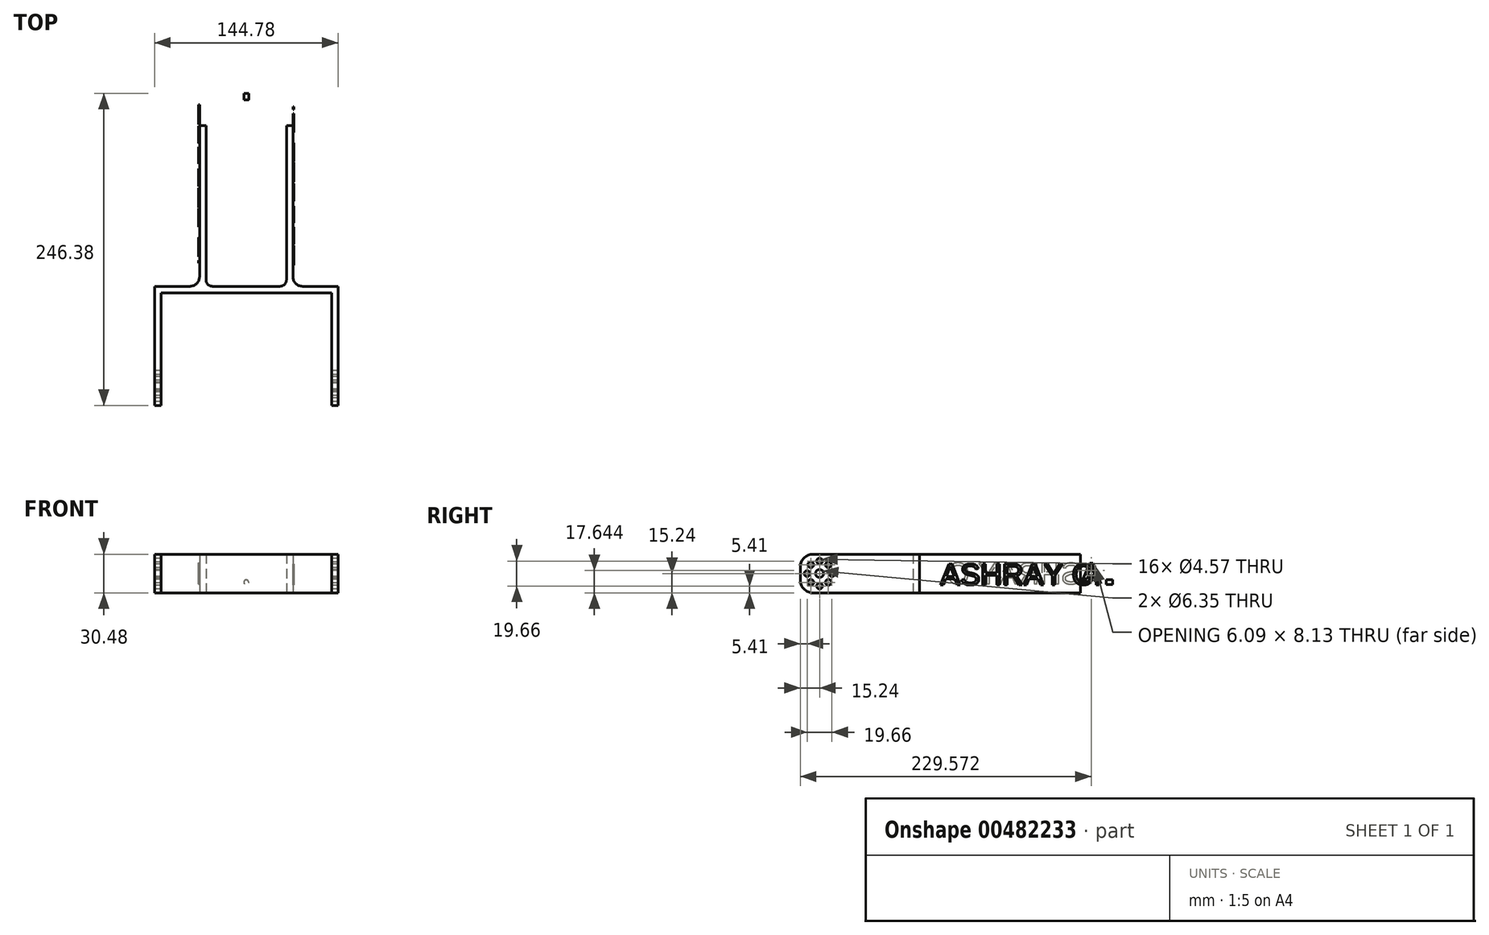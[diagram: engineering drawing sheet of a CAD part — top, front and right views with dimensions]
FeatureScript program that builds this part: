
annotation { "Feature Type Name" : "Feature", "Feature Type Description" : "" }
export const myFeature = defineFeature(function(context is Context, id is Id, definition is map)
    precondition{}
    {
        {
            var Q0;
            Q0=qCreatedBy(makeId("Top.planeOp"),FACE);
            var sketch = newSketch(context, id + "F0", { "sketchPlane" : qUnion([Q0])});
            skLineSegment(sketch, "E0.bottom", {"start": v(67.31, -2.54) * mm, "end": v(-67.31, -2.54) * mm});
            skLineSegment(sketch, "E0.top", {"start": v(67.31, 2.54) * mm, "end": v(-67.31, 2.54) * mm});
            skLineSegment(sketch, "E0.left", {"start": v(67.31, -2.54) * mm, "end": v(67.31, 2.54) * mm});
            skLineSegment(sketch, "E0.right", {"start": v(-67.31, -2.54) * mm, "end": v(-67.31, 2.54) * mm});
            skPoint(sketch, "E0.middle", {"position": v(0, 0) * mm});
            skLineSegment(sketch, "E1.bottom", {"start": v(-67.3, -91.44) * mm, "end": v(-72.4, -91.44) * mm});
            skLineSegment(sketch, "E1.top", {"start": v(-67.31, 154.94) * mm, "end": v(-72.4, 154.94) * mm});
            skLineSegment(sketch, "E1.left", {"start": v(-67.31, -91.44) * mm, "end": v(-67.31, 154.94) * mm});
            skLineSegment(sketch, "E1.right", {"start": v(-72.4, -91.44) * mm, "end": v(-72.4, 154.94) * mm});
            skLineSegment(sketch, "E2.bottom", {"start": v(67.31, -91.44) * mm, "end": v(72.4, -91.44) * mm});
            skLineSegment(sketch, "E2.top", {"start": v(67.31, 154.94) * mm, "end": v(72.4, 154.94) * mm});
            skLineSegment(sketch, "E2.left", {"start": v(67.31, -91.44) * mm, "end": v(67.31, 154.94) * mm});
            skLineSegment(sketch, "E2.right", {"start": v(72.4, -91.44) * mm, "end": v(72.4, 154.94) * mm});
            skLineSegment(sketch, "E3.bottom", {"start": v(-36.83, 2.54) * mm, "end": v(-31.75, 2.54) * mm});
            skLineSegment(sketch, "E3.top", {"start": v(-36.83, 154.94) * mm, "end": v(-31.75, 154.94) * mm});
            skLineSegment(sketch, "E3.left", {"start": v(-36.83, 2.54) * mm, "end": v(-36.83, 154.94) * mm});
            skLineSegment(sketch, "E3.right", {"start": v(-31.75, 2.54) * mm, "end": v(-31.75, 154.94) * mm});
            skLineSegment(sketch, "E4.bottom", {"start": v(31.75, 2.54) * mm, "end": v(36.83, 2.54) * mm});
            skLineSegment(sketch, "E4.top", {"start": v(31.75, 154.94) * mm, "end": v(36.83, 154.94) * mm});
            skLineSegment(sketch, "E4.left", {"start": v(31.75, 2.54) * mm, "end": v(31.75, 154.94) * mm});
            skLineSegment(sketch, "E4.right", {"start": v(36.83, 2.54) * mm, "end": v(36.83, 154.94) * mm});
            skLineSegment(sketch, "E5", {"start": v(-36.83, 154.94) * mm, "end": v(36.83, 154.94) * mm});
            skLineSegment(sketch, "E6", {"start": v(-67.31, 2.54) * mm, "end": v(-72.4, 2.54) * mm});
            skLineSegment(sketch, "E7", {"start": v(67.31, 2.54) * mm, "end": v(72.4, 2.54) * mm});
            skSolve(sketch);
        }
        {
            var Q0;
            Q0=makeQuery(id+"F0.imprint","IMPRINT",FACE,{"disambiguationData":[TD([[makeQuery(id+"F0.imprint","IMPRINT",EDGE,{"derivedFrom":sQuery(id+"F0.wireOp",EDGE,"E3.top")}),-1.0]])]});
            var Q1;
            Q1=makeQuery(id+"F0.imprint","IMPRINT",FACE,{"disambiguationData":[TD([[makeQuery(id+"F0.imprint","IMPRINT",EDGE,{"derivedFrom":sQuery(id+"F0.wireOp",EDGE,"E4.top")}),-1.0]])]});
            var Q2;
            Q2=makeQuery(id+"F0.imprint","IMPRINT",FACE,{"disambiguationData":[TD([[makeQuery(id+"F0.imprint","IMPRINT",EDGE,{"derivedFrom":sQuery(id+"F0.wireOp",EDGE,"E0.bottom")}),-1.0]])]});
            var Q3;
            {var subQ1=sQuery(id+"F0.wireOp",EDGE,"E0.left");Q3=makeQuery(id+"F0.imprint","IMPRINT",FACE,{"disambiguationData":[TD([[makeQuery(id+"F0.imprint","IMPRINT",EDGE,{"derivedFrom":subQ1}),-1.0]])]});}
            var Q4;
            {var subQ1=sQuery(id+"F0.wireOp",EDGE,"E0.right");Q4=makeQuery(id+"F0.imprint","IMPRINT",FACE,{"disambiguationData":[TD([[makeQuery(id+"F0.imprint","IMPRINT",EDGE,{"derivedFrom":subQ1}),1.0]])]});}
            extrude(context, id + "F1", {"entities" : qUnion([Q0, Q1, Q2, Q3, Q4]), "depth" : 30.48 * mm});
        }
        {
            var Q0;
            Q0=makeQuery(id+"F1.opExtrude","SWEPT_FACE",FACE,{"disambiguationData":[OSD([sQuery(id+"F0.wireOp",EDGE,"E3.right")])]});
            var sketch = newSketch(context, id + "F2", { "sketchPlane" : qUnion([Q0])});
            skLineSegment(sketch, "E8.bottom", {"start": v(154.94, 30.48) * mm, "end": v(149.86, 30.48) * mm});
            skLineSegment(sketch, "E8.top", {"start": v(154.94, 0) * mm, "end": v(149.86, 0) * mm});
            skLineSegment(sketch, "E8.left", {"start": v(154.94, 30.48) * mm, "end": v(154.94, 0) * mm});
            skLineSegment(sketch, "E8.right", {"start": v(149.86, 30.48) * mm, "end": v(149.86, 0) * mm});
            skSolve(sketch);
        }
        {
            var Q0;
            Q0=makeQuery(id+"F2.imprint","IMPRINT",FACE,{"disambiguationData":[TD([[makeQuery(id+"F2.imprint","IMPRINT",EDGE,{"derivedFrom":sQuery(id+"F2.wireOp",EDGE,"E8.bottom")}),-1.0]])]});
            extrude(context, id + "F3", {"entities" : qUnion([Q0]), "operationType" : NewBodyOperationType.ADD, "depth" : 66.04 * mm});
        }
        {
            var Q0;
            Q0=makeQuery(id+"F1.opExtrude","SWEPT_EDGE",EDGE,{"disambiguationData":[OSD([sQuery(id+"F0.wireOp",EDGE,"E0.top"),sQuery(id+"F0.wireOp",EDGE,"E3.left")])]});
            var Q1;
            Q1=makeQuery(id+"F1.opExtrude","SWEPT_EDGE",EDGE,{"disambiguationData":[OSD([sQuery(id+"F0.wireOp",EDGE,"E0.top"),sQuery(id+"F0.wireOp",EDGE,"E4.right")])]});
            fillet(context, id + "F4", {"entities" : qUnion([Q0, Q1]), "radius" : 7.62 * mm, "tangentPropagation" : true, "allowEdgeOverflow" : false});
        }
        {
            var Q0;
            Q0=makeQuery(id+"F1.opExtrude","SWEPT_EDGE",EDGE,{"disambiguationData":[OSD([sQuery(id+"F0.wireOp",EDGE,"E0.top"),sQuery(id+"F0.wireOp",EDGE,"E3.right")])]});
            var Q1;
            Q1=makeQuery(id+"F1.opExtrude","SWEPT_EDGE",EDGE,{"disambiguationData":[OSD([sQuery(id+"F0.wireOp",EDGE,"E0.top"),sQuery(id+"F0.wireOp",EDGE,"E4.left")])]});
            fillet(context, id + "F5", {"entities" : qUnion([Q0, Q1]), "radius" : 5.08 * mm, "tangentPropagation" : true, "allowEdgeOverflow" : false});
        }
        {
            var Q0;
            Q0=makeQuery(id+"F1.opExtrude","SWEPT_FACE",FACE,{"disambiguationData":[OSD([sQuery(id+"F0.wireOp",EDGE,"E1.right")])]});
            var sketch = newSketch(context, id + "F6", { "sketchPlane" : qUnion([Q0])});
            skCircle(sketch, "E9", {"center": v(76.2, 15.24) * mm, "radius": 12.7 * mm});
            skCircle(sketch, "E10", {"center": v(66.37, 15.24) * mm, "radius": 2.29 * mm});
            skCircle(sketch, "E11", {"center": v(76.2, 25.07) * mm, "radius": 2.29 * mm});
            skCircle(sketch, "E12", {"center": v(86.03, 15.24) * mm, "radius": 2.29 * mm});
            skCircle(sketch, "E13", {"center": v(76.2, 5.41) * mm, "radius": 2.29 * mm});
            skCircle(sketch, "E14", {"center": v(76.2, 15.24) * mm, "radius": 3.18 * mm});
            skLineSegment(sketch, "E15", {"start": v(66.37, 15.24) * mm, "end": v(86.03, 15.24) * mm});
            skLineSegment(sketch, "E16", {"start": v(76.2, 25.07) * mm, "end": v(76.2, 5.41) * mm});
            skCircle(sketch, "E17", {"center": v(69.25, 8.29) * mm, "radius": 2.29 * mm});
            skCircle(sketch, "E18", {"center": v(83.15, 22.2) * mm, "radius": 2.29 * mm});
            skCircle(sketch, "E19", {"center": v(69.25, 22.2) * mm, "radius": 2.29 * mm});
            skCircle(sketch, "E20", {"center": v(83.15, 8.29) * mm, "radius": 2.29 * mm});
            skLineSegment(sketch, "E21", {"start": v(69.25, 8.29) * mm, "end": v(83.15, 22.2) * mm});
            skLineSegment(sketch, "E22", {"start": v(69.25, 22.2) * mm, "end": v(83.15, 8.29) * mm});
            skSolve(sketch);
        }
        {
            var Q0;
            Q0=makeQuery(id+"F6.imprint","IMPRINT",FACE,{"disambiguationData":[TD([[makeQuery(id+"F6.imprint","IMPRINT",EDGE,{"derivedFrom":sQuery(id+"F6.wireOp",EDGE,"E18")}),1.0]])]});
            var Q1;
            Q1=makeQuery(id+"F6.imprint","IMPRINT",FACE,{"disambiguationData":[TD([[makeQuery(id+"F6.imprint","IMPRINT",EDGE,{"derivedFrom":sQuery(id+"F6.wireOp",EDGE,"E11")}),1.0]])]});
            var Q2;
            Q2=makeQuery(id+"F6.imprint","IMPRINT",FACE,{"disambiguationData":[TD([[makeQuery(id+"F6.imprint","IMPRINT",EDGE,{"derivedFrom":sQuery(id+"F6.wireOp",EDGE,"E19")}),1.0]])]});
            var Q3;
            Q3=makeQuery(id+"F6.imprint","IMPRINT",FACE,{"disambiguationData":[TD([[makeQuery(id+"F6.imprint","IMPRINT",EDGE,{"derivedFrom":sQuery(id+"F6.wireOp",EDGE,"E10")}),1.0]])]});
            var Q4;
            Q4=makeQuery(id+"F6.imprint","IMPRINT",FACE,{"disambiguationData":[TD([[makeQuery(id+"F6.imprint","IMPRINT",EDGE,{"derivedFrom":sQuery(id+"F6.wireOp",EDGE,"E17")}),1.0]])]});
            var Q5;
            Q5=makeQuery(id+"F6.imprint","IMPRINT",FACE,{"disambiguationData":[TD([[makeQuery(id+"F6.imprint","IMPRINT",EDGE,{"derivedFrom":sQuery(id+"F6.wireOp",EDGE,"E13")}),1.0]])]});
            var Q6;
            Q6=makeQuery(id+"F6.imprint","IMPRINT",FACE,{"disambiguationData":[TD([[makeQuery(id+"F6.imprint","IMPRINT",EDGE,{"derivedFrom":sQuery(id+"F6.wireOp",EDGE,"E20")}),1.0]])]});
            var Q7;
            Q7=makeQuery(id+"F6.imprint","IMPRINT",FACE,{"disambiguationData":[TD([[makeQuery(id+"F6.imprint","IMPRINT",EDGE,{"derivedFrom":sQuery(id+"F6.wireOp",EDGE,"E12")}),1.0]])]});
            var Q8;
            {var subQ0=sQuery(id+"F6.wireOp",EDGE,"E16");var subQ1=sQuery(id+"F6.wireOp",EDGE,"E14");var subQ2=makeQuery(id+"F6.imprint","INTERSECT",VERTEX,{"disambiguationData":[OD(1.0)],"derivedFrom":[subQ1,subQ0]});Q8=makeQuery(id+"F6.imprint","IMPRINT",FACE,{"disambiguationData":[TD([[makeQuery(id+"F6.imprint","IMPRINT",EDGE,{"disambiguationData":[TD([[subQ2,-1.0]])],"derivedFrom":subQ1}),1.0]])]});}
            var Q9;
            {var subQ0=sQuery(id+"F6.wireOp",EDGE,"E15");var subQ1=sQuery(id+"F6.wireOp",EDGE,"E14");var subQ2=makeQuery(id+"F6.imprint","INTERSECT",VERTEX,{"disambiguationData":[OD(0.0)],"derivedFrom":[subQ1,subQ0]});Q9=makeQuery(id+"F6.imprint","IMPRINT",FACE,{"disambiguationData":[TD([[makeQuery(id+"F6.imprint","IMPRINT",EDGE,{"disambiguationData":[TD([[subQ2,1.0]])],"derivedFrom":subQ1}),1.0]])]});}
            var Q10;
            {var subQ0=sQuery(id+"F6.wireOp",EDGE,"E21");var subQ1=sQuery(id+"F6.wireOp",EDGE,"E14");var subQ2=makeQuery(id+"F6.imprint","INTERSECT",VERTEX,{"disambiguationData":[OD(0.0)],"derivedFrom":[subQ1,subQ0]});Q10=makeQuery(id+"F6.imprint","IMPRINT",FACE,{"disambiguationData":[TD([[makeQuery(id+"F6.imprint","IMPRINT",EDGE,{"disambiguationData":[TD([[subQ2,1.0]])],"derivedFrom":subQ1}),1.0]])]});}
            var Q11;
            {var subQ0=sQuery(id+"F6.wireOp",EDGE,"E21");var subQ1=sQuery(id+"F6.wireOp",EDGE,"E14");var subQ2=makeQuery(id+"F6.imprint","INTERSECT",VERTEX,{"disambiguationData":[OD(0.0)],"derivedFrom":[subQ1,subQ0]});Q11=makeQuery(id+"F6.imprint","IMPRINT",FACE,{"disambiguationData":[TD([[makeQuery(id+"F6.imprint","IMPRINT",EDGE,{"disambiguationData":[TD([[subQ2,-1.0]])],"derivedFrom":subQ1}),1.0]])]});}
            var Q12;
            {var subQ0=sQuery(id+"F6.wireOp",EDGE,"E16");var subQ1=sQuery(id+"F6.wireOp",EDGE,"E14");var subQ2=makeQuery(id+"F6.imprint","INTERSECT",VERTEX,{"disambiguationData":[OD(0.0)],"derivedFrom":[subQ1,subQ0]});Q12=makeQuery(id+"F6.imprint","IMPRINT",FACE,{"disambiguationData":[TD([[makeQuery(id+"F6.imprint","IMPRINT",EDGE,{"disambiguationData":[TD([[subQ2,-1.0]])],"derivedFrom":subQ1}),1.0]])]});}
            var Q13;
            {var subQ0=sQuery(id+"F6.wireOp",EDGE,"E22");var subQ1=sQuery(id+"F6.wireOp",EDGE,"E14");var subQ2=makeQuery(id+"F6.imprint","INTERSECT",VERTEX,{"disambiguationData":[OD(0.0)],"derivedFrom":[subQ1,subQ0]});Q13=makeQuery(id+"F6.imprint","IMPRINT",FACE,{"disambiguationData":[TD([[makeQuery(id+"F6.imprint","IMPRINT",EDGE,{"disambiguationData":[TD([[subQ2,-1.0]])],"derivedFrom":subQ1}),1.0]])]});}
            var Q14;
            {var subQ0=sQuery(id+"F6.wireOp",EDGE,"E15");var subQ1=sQuery(id+"F6.wireOp",EDGE,"E14");var subQ2=makeQuery(id+"F6.imprint","INTERSECT",VERTEX,{"disambiguationData":[OD(1.0)],"derivedFrom":[subQ1,subQ0]});Q14=makeQuery(id+"F6.imprint","IMPRINT",FACE,{"disambiguationData":[TD([[makeQuery(id+"F6.imprint","IMPRINT",EDGE,{"disambiguationData":[TD([[subQ2,-1.0]])],"derivedFrom":subQ1}),1.0]])]});}
            var Q15;
            {var subQ0=sQuery(id+"F6.wireOp",EDGE,"E21");var subQ1=sQuery(id+"F6.wireOp",EDGE,"E14");var subQ2=makeQuery(id+"F6.imprint","INTERSECT",VERTEX,{"disambiguationData":[OD(1.0)],"derivedFrom":[subQ1,subQ0]});Q15=makeQuery(id+"F6.imprint","IMPRINT",FACE,{"disambiguationData":[TD([[makeQuery(id+"F6.imprint","IMPRINT",EDGE,{"disambiguationData":[TD([[subQ2,-1.0]])],"derivedFrom":subQ1}),1.0]])]});}
            extrude(context, id + "F7", {"entities" : qUnion([Q0, Q1, Q2, Q3, Q4, Q5, Q6, Q7, Q8, Q9, Q10, Q11, Q12, Q13, Q14, Q15]), "operationType" : NewBodyOperationType.REMOVE, "oppositeDirection" : true, "depth" : 254 * mm, "offsetDistance" : 25.4 * mm});
        }
        {
            var Q0;
            Q0=makeQuery(id+"F1.opExtrude","CAP_EDGE",EDGE,{"disambiguationData":[OSD([sQuery(id+"F0.wireOp",EDGE,"E2.bottom")])],"isStart":true});
            var Q1;
            Q1=makeQuery(id+"F1.opExtrude","CAP_EDGE",EDGE,{"disambiguationData":[OSD([sQuery(id+"F0.wireOp",EDGE,"E2.bottom")])],"isStart":false});
            var Q2;
            Q2=makeQuery(id+"F1.opExtrude","CAP_EDGE",EDGE,{"disambiguationData":[OSD([sQuery(id+"F0.wireOp",EDGE,"E1.bottom")])],"isStart":true});
            var Q3;
            Q3=makeQuery(id+"F1.opExtrude","CAP_EDGE",EDGE,{"disambiguationData":[OSD([sQuery(id+"F0.wireOp",EDGE,"E1.bottom")])],"isStart":false});
            fillet(context, id + "F8", {"entities" : qUnion([Q0, Q1, Q2, Q3]), "radius" : 10.16 * mm, "tangentPropagation" : true, "allowEdgeOverflow" : false});
        }
        {
            var Q0;
            Q0=makeQuery(id+"F1.opExtrude","SWEPT_FACE",FACE,{"disambiguationData":[OSD([sQuery(id+"F0.wireOp",EDGE,"E4.right")])]});
            var sketch = newSketch(context, id + "F9", { "sketchPlane" : qUnion([Q0])});
            skText(sketch, "E23", { "text": "ASHRAY C.", "fontName": "Arimo-Regular.ttf"});
            const initialGuessF9  = {"E23": [0.01905, 0.00635, 1, 0, 0.01703]};
            skSetInitialGuess(sketch, initialGuessF9);
            skSolve(sketch);
        }
        {
            var Q0;
            Q0=makeQuery(id+"F1.opExtrude","SWEPT_FACE",FACE,{"disambiguationData":[OSD([sQuery(id+"F0.wireOp",EDGE,"E3.left")])]});
            var sketch = newSketch(context, id + "F10", { "sketchPlane" : qUnion([Q0])});
            skText(sketch, "E24", { "text": "ASHRAY C.", "fontName": "Arimo-Regular.ttf"});
            const initialGuessF10  = {"E24": [-0.14605, 0.0071, 1, 0, 0.01703]};
            skSetInitialGuess(sketch, initialGuessF10);
            skSolve(sketch);
        }
        {
            var Q0;
            Q0=makeQuery(id+"F9.imprint","IMPRINT",FACE,{"disambiguationData":[TD([[makeQuery(id+"F9.imprint","IMPRINT",EDGE,{"derivedFrom":sQuery(id+"F9.wireOp",EDGE,"E23.sketch_text.stroke-0")}),-1.0]])]});
            var Q1;
            Q1=makeQuery(id+"F9.imprint","IMPRINT",FACE,{"disambiguationData":[TD([[makeQuery(id+"F9.imprint","IMPRINT",EDGE,{"derivedFrom":sQuery(id+"F9.wireOp",EDGE,"E23.sketch_text.stroke-15")}),-1.0]])]});
            var Q2;
            Q2=makeQuery(id+"F9.imprint","IMPRINT",FACE,{"disambiguationData":[TD([[makeQuery(id+"F9.imprint","IMPRINT",EDGE,{"derivedFrom":sQuery(id+"F9.wireOp",EDGE,"E23.sketch_text.stroke-49")}),-1.0]])]});
            var Q3;
            Q3=makeQuery(id+"F9.imprint","IMPRINT",FACE,{"disambiguationData":[TD([[makeQuery(id+"F9.imprint","IMPRINT",EDGE,{"derivedFrom":sQuery(id+"F9.wireOp",EDGE,"E23.sketch_text.stroke-61")}),-1.0]])]});
            var Q4;
            Q4=makeQuery(id+"F9.imprint","IMPRINT",FACE,{"disambiguationData":[TD([[makeQuery(id+"F9.imprint","IMPRINT",EDGE,{"derivedFrom":sQuery(id+"F9.wireOp",EDGE,"E23.sketch_text.stroke-80")}),-1.0]])]});
            var Q5;
            Q5=makeQuery(id+"F9.imprint","IMPRINT",FACE,{"disambiguationData":[TD([[makeQuery(id+"F9.imprint","IMPRINT",EDGE,{"derivedFrom":sQuery(id+"F9.wireOp",EDGE,"E23.sketch_text.stroke-95")}),-1.0]])]});
            var Q6;
            Q6=makeQuery(id+"F9.imprint","IMPRINT",FACE,{"disambiguationData":[TD([[makeQuery(id+"F9.imprint","IMPRINT",EDGE,{"derivedFrom":sQuery(id+"F9.wireOp",EDGE,"E23.sketch_text.stroke-104")}),-1.0]])]});
            var Q7;
            Q7=makeQuery(id+"F9.imprint","IMPRINT",FACE,{"disambiguationData":[TD([[makeQuery(id+"F9.imprint","IMPRINT",EDGE,{"derivedFrom":sQuery(id+"F9.wireOp",EDGE,"E23.sketch_text.stroke-122")}),-1.0]])]});
            extrude(context, id + "F11", {"entities" : qUnion([Q0, Q1, Q2, Q3, Q4, Q5, Q6, Q7]), "operationType" : NewBodyOperationType.ADD, "depth" : 0.76 * mm, "offsetDistance" : 25.4 * mm});
        }
        {
            var Q0;
            Q0=makeQuery(id+"F10.imprint","IMPRINT",FACE,{"disambiguationData":[TD([[makeQuery(id+"F10.imprint","IMPRINT",EDGE,{"derivedFrom":sQuery(id+"F10.wireOp",EDGE,"E24.sketch_text.stroke-0")}),-1.0]])]});
            var Q1;
            Q1=makeQuery(id+"F10.imprint","IMPRINT",FACE,{"disambiguationData":[TD([[makeQuery(id+"F10.imprint","IMPRINT",EDGE,{"derivedFrom":sQuery(id+"F10.wireOp",EDGE,"E24.sketch_text.stroke-15")}),-1.0]])]});
            var Q2;
            Q2=makeQuery(id+"F10.imprint","IMPRINT",FACE,{"disambiguationData":[TD([[makeQuery(id+"F10.imprint","IMPRINT",EDGE,{"derivedFrom":sQuery(id+"F10.wireOp",EDGE,"E24.sketch_text.stroke-49")}),-1.0]])]});
            var Q3;
            Q3=makeQuery(id+"F10.imprint","IMPRINT",FACE,{"disambiguationData":[TD([[makeQuery(id+"F10.imprint","IMPRINT",EDGE,{"derivedFrom":sQuery(id+"F10.wireOp",EDGE,"E24.sketch_text.stroke-61")}),-1.0]])]});
            var Q4;
            Q4=makeQuery(id+"F10.imprint","IMPRINT",FACE,{"disambiguationData":[TD([[makeQuery(id+"F10.imprint","IMPRINT",EDGE,{"derivedFrom":sQuery(id+"F10.wireOp",EDGE,"E24.sketch_text.stroke-80")}),-1.0]])]});
            var Q5;
            Q5=makeQuery(id+"F10.imprint","IMPRINT",FACE,{"disambiguationData":[TD([[makeQuery(id+"F10.imprint","IMPRINT",EDGE,{"derivedFrom":sQuery(id+"F10.wireOp",EDGE,"E24.sketch_text.stroke-95")}),-1.0]])]});
            var Q6;
            Q6=makeQuery(id+"F10.imprint","IMPRINT",FACE,{"disambiguationData":[TD([[makeQuery(id+"F10.imprint","IMPRINT",EDGE,{"derivedFrom":sQuery(id+"F10.wireOp",EDGE,"E24.sketch_text.stroke-104")}),-1.0]])]});
            var Q7;
            Q7=makeQuery(id+"F10.imprint","IMPRINT",FACE,{"disambiguationData":[TD([[makeQuery(id+"F10.imprint","IMPRINT",EDGE,{"derivedFrom":sQuery(id+"F10.wireOp",EDGE,"E24.sketch_text.stroke-122")}),-1.0]])]});
            extrude(context, id + "F12", {"entities" : qUnion([Q0, Q1, Q2, Q3, Q4, Q5, Q6, Q7]), "operationType" : NewBodyOperationType.ADD, "depth" : 0.76 * mm, "offsetDistance" : 25.4 * mm});
        }
        {
            var Q0;
            Q0=makeQuery(id+"F3.boolean.opBoolean","MERGE",FACE,{"derivedFrom":[makeQuery(id+"F1.opExtrude","SWEPT_FACE",FACE,{"disambiguationData":[OSD([sQuery(id+"F0.wireOp",EDGE,"E3.top")])]}),makeQuery(id+"F1.opExtrude","SWEPT_FACE",FACE,{"disambiguationData":[OSD([sQuery(id+"F0.wireOp",EDGE,"E4.top")])]}),makeQuery(id+"F3.opExtrude","SWEPT_FACE",FACE,{"disambiguationData":[OSD([sQuery(id+"F2.wireOp",EDGE,"E8.left")])]})]});
            var sketch = newSketch(context, id + "F13", { "sketchPlane" : qUnion([Q0])});
            skCircle(sketch, "E25", {"center": v(0, 15.24) * mm, "radius": 4.25 * mm});
            skCircle(sketch, "E26", {"center": v(6.92, 15.24) * mm, "radius": 1.9 * mm});
            skCircle(sketch, "E27", {"center": v(0, 22.16) * mm, "radius": 1.9 * mm});
            skCircle(sketch, "E28", {"center": v(-6.92, 15.24) * mm, "radius": 1.9 * mm});
            skCircle(sketch, "E29", {"center": v(0, 8.32) * mm, "radius": 1.9 * mm});
            skSolve(sketch);
        }
        {
            var Q0;
            Q0=makeQuery(id+"F13.imprint","IMPRINT",FACE,{"disambiguationData":[TD([[makeQuery(id+"F13.imprint","IMPRINT",EDGE,{"derivedFrom":sQuery(id+"F13.wireOp",EDGE,"E28")}),1.0]])]});
            var Q1;
            Q1=makeQuery(id+"F13.imprint","IMPRINT",FACE,{"disambiguationData":[TD([[makeQuery(id+"F13.imprint","IMPRINT",EDGE,{"derivedFrom":sQuery(id+"F13.wireOp",EDGE,"E25")}),1.0]])]});
            var Q2;
            Q2=makeQuery(id+"F13.imprint","IMPRINT",FACE,{"disambiguationData":[TD([[makeQuery(id+"F13.imprint","IMPRINT",EDGE,{"derivedFrom":sQuery(id+"F13.wireOp",EDGE,"E27")}),1.0]])]});
            var Q3;
            Q3=makeQuery(id+"F13.imprint","IMPRINT",FACE,{"disambiguationData":[TD([[makeQuery(id+"F13.imprint","IMPRINT",EDGE,{"derivedFrom":sQuery(id+"F13.wireOp",EDGE,"E26")}),1.0]])]});
            var Q4;
            Q4=makeQuery(id+"F13.imprint","IMPRINT",FACE,{"disambiguationData":[TD([[makeQuery(id+"F13.imprint","IMPRINT",EDGE,{"derivedFrom":sQuery(id+"F13.wireOp",EDGE,"E29")}),-1.0]])]});
            extrude(context, id + "F14", {"entities" : qUnion([Q0, Q1, Q2, Q3, Q4]), "operationType" : NewBodyOperationType.REMOVE, "oppositeDirection" : true, "depth" : 25.4 * mm});
        }
    });
